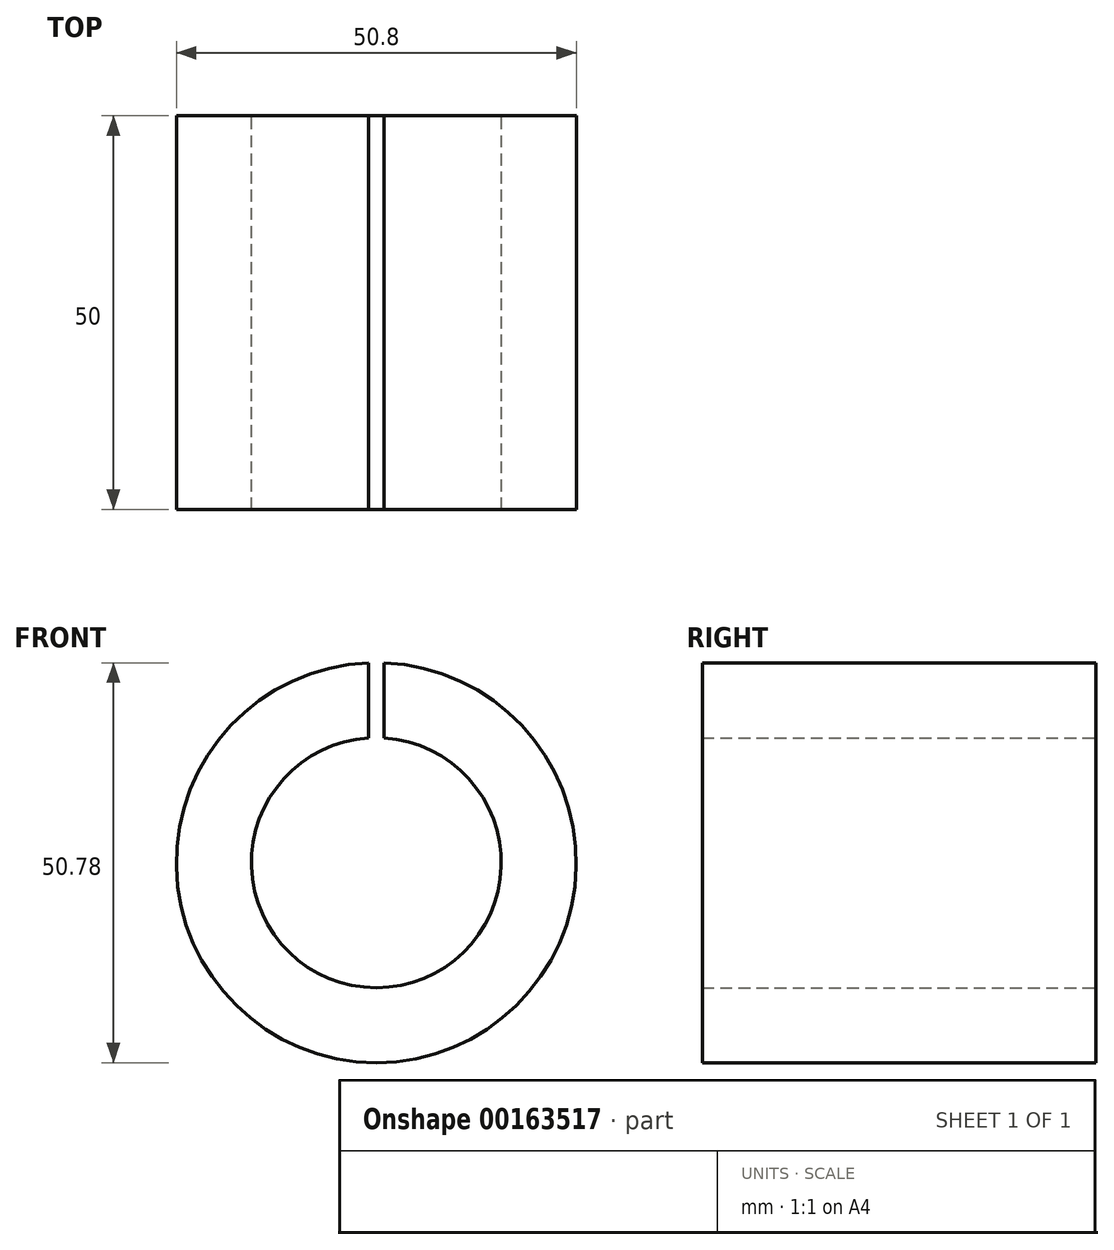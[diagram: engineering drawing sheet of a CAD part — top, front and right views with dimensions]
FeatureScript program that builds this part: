
annotation { "Feature Type Name" : "Feature", "Feature Type Description" : "" }
export const myFeature = defineFeature(function(context is Context, id is Id, definition is map)
    precondition{}
    {
        {
            var Q0;
            Q0=qCreatedBy(makeId("Front.planeOp"),FACE);
            var sketch = newSketch(context, id + "F0", { "sketchPlane" : qUnion([Q0])});
            skArc(sketch, "E0", {"start": v(-1, 25.38) * mm, "mid": v(0, -25.4) * mm, "end": v(1, 25.38) * mm});
            skArc(sketch, "E1", {"start": v(-1, 15.84) * mm, "mid": v(0, -15.87) * mm, "end": v(1, 15.84) * mm});
            skLineSegment(sketch, "E2", {"start": v(-1, 25.38) * mm, "end": v(-1, 15.84) * mm});
            skLineSegment(sketch, "E3", {"start": v(1, 25.38) * mm, "end": v(1, 15.84) * mm});
            skSolve(sketch);
        }
        {
            var Q0;
            Q0 = qSketchRegion(id + "F0", true);
            extrude(context, id + "F1", {"entities" : qUnion([Q0]), "endBound" : BoundingType.SYMMETRIC, "depth" : 50 * mm});
        }
    });
